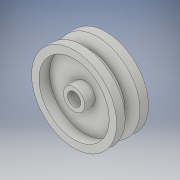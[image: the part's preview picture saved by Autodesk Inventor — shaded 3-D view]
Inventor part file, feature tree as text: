
AUTODESK INVENTOR PART (.ipt)
format: ipt  version: 2019 (Build 230136000, 136)  size: 150,016 bytes
history: native  units: in
note: dims shown in document units (in); Inventor stores cm internally (conversion verified against a paired STEP export)
features: revolve x1, sketch x1
ambient origin geometry x8: Origin, YZ Plane, XZ Plane, XY Plane, X Axis, Y Axis, Z Axis, Center Point
bodies: Solid1 (feature_tree)
feature tree (2):
  revolve  "Revolution1"  [1 undecoded]
  sketch  "Sketch1"  dims[d3=0.4in d4=0.4in d6=2.0in d8=1.65in d9=0.5in d10=0.5in d13=0.5in d14=0.4in d15=90.0deg d16=0.4in d17=90.0deg]
note: 1 required parameter value undecoded (feature->parameter linkage not recoverable at this tier; creation-order binding heuristic only, values carry confidence <= 0.55)
